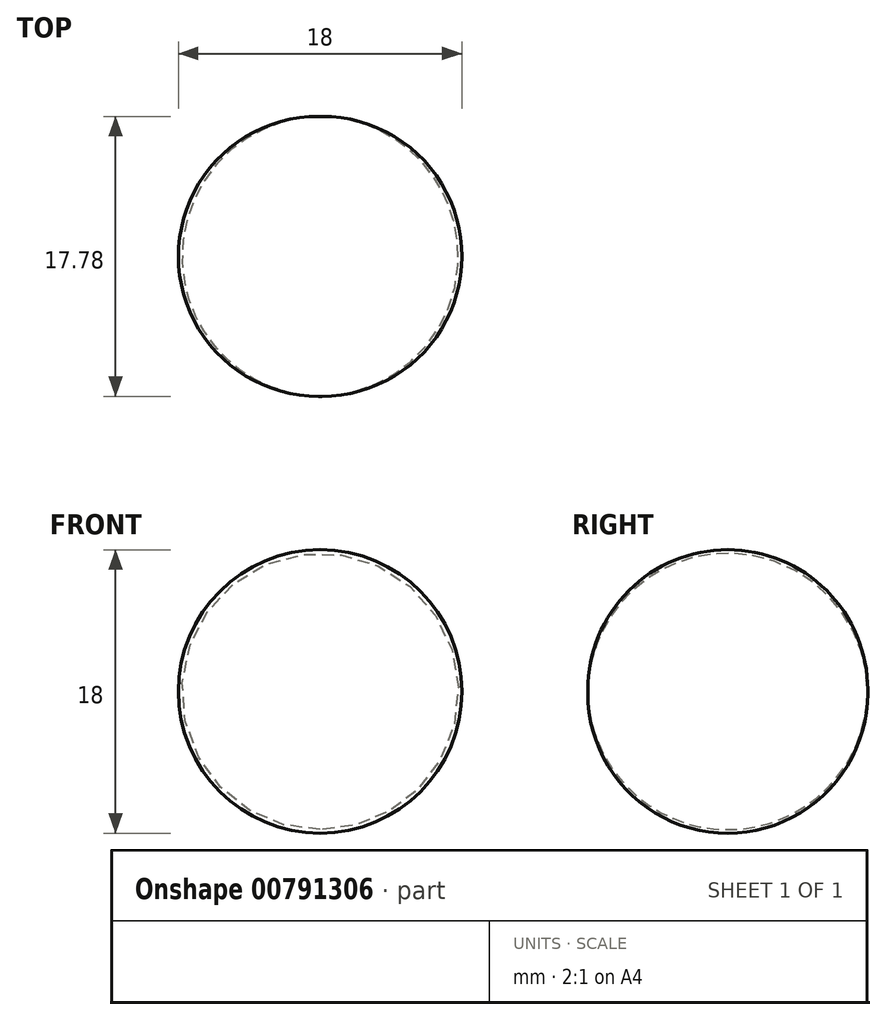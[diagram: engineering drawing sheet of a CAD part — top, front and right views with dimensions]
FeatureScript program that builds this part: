
annotation { "Feature Type Name" : "Feature", "Feature Type Description" : "" }
export const myFeature = defineFeature(function(context is Context, id is Id, definition is map)
    precondition{}
    {
        {
            var Q0;
            Q0=qCreatedBy(makeId("Top.planeOp"),FACE);
            var sketch = newSketch(context, id + "F0", { "sketchPlane" : qUnion([Q0])});
            skArc(sketch, "E0", {"start": v(0, 5.22) * mm, "mid": v(-9, -3.67) * mm, "end": v(0, -12.56) * mm});
            skLineSegment(sketch, "E1", {"start": v(0, 5.22) * mm, "end": v(0, -12.56) * mm});
            skSolve(sketch);
        }
        {
            var Q0;
            Q0 = qSketchRegion(id + "F0", true);
            var Q1;
            Q1=sQuery(id+"F0.wireOp",EDGE,"E1");
            revolve(context, id + "F1", {"surfaceOperationType" : NewSurfaceOperationType.NEW, "entities" : qUnion([Q0]), "axis" : qUnion([Q1]), "revolveType" : RevolveType.FULL});
        }
    });
